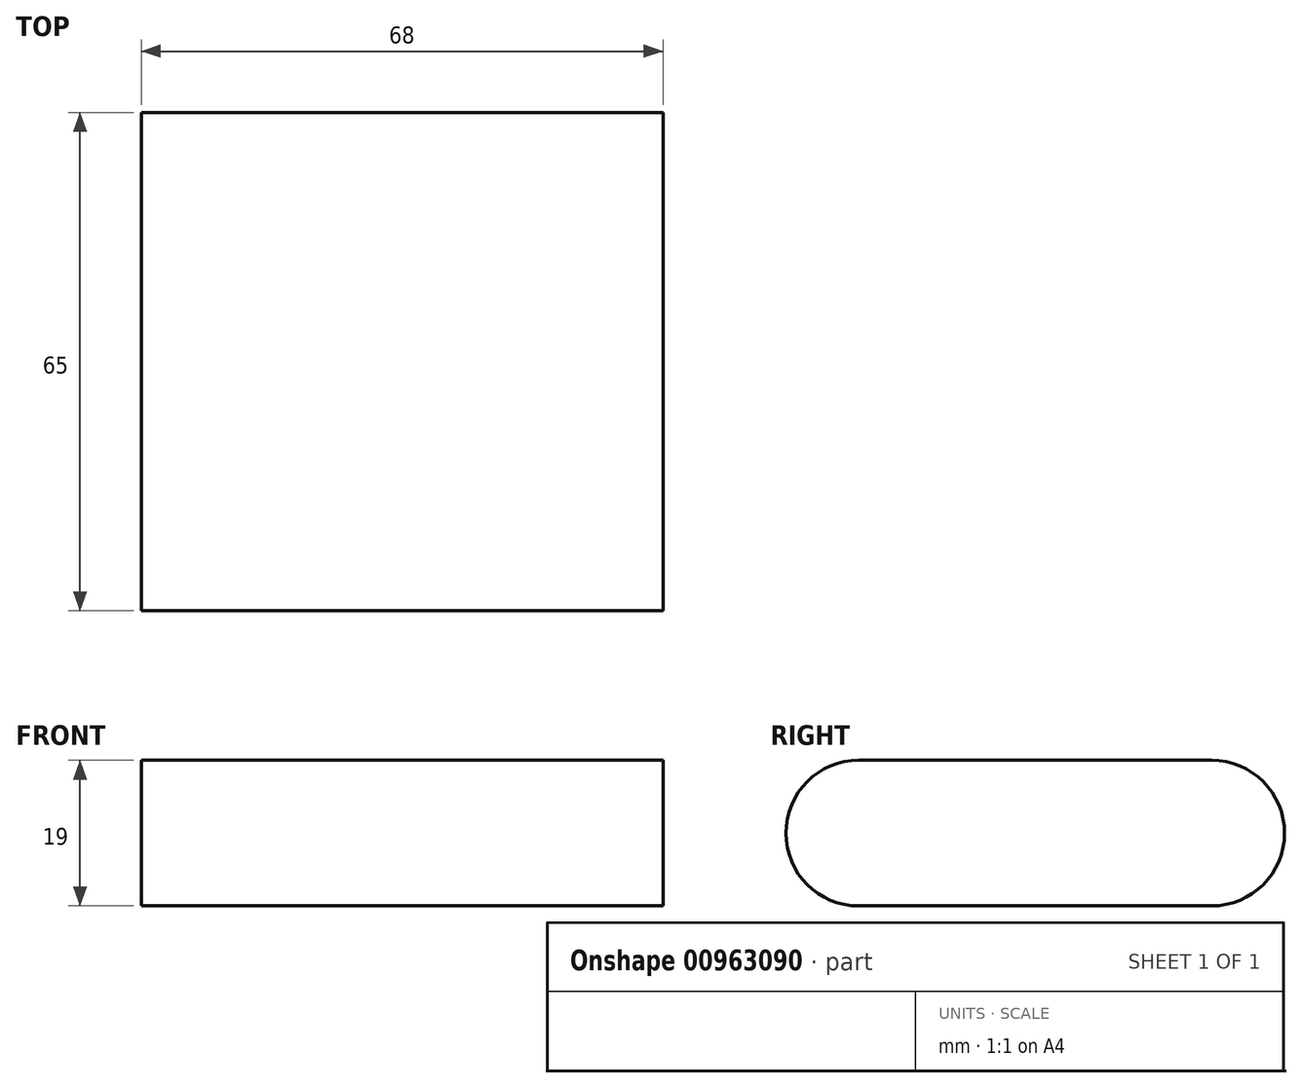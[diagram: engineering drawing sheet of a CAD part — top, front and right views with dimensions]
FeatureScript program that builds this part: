
annotation { "Feature Type Name" : "Feature", "Feature Type Description" : "" }
export const myFeature = defineFeature(function(context is Context, id is Id, definition is map)
    precondition{}
    {
        {
            var Q0;
            Q0=qCreatedBy(makeId("Right.planeOp"),FACE);
            var sketch = newSketch(context, id + "F0", { "sketchPlane" : qUnion([Q0])});
            skLineSegment(sketch, "E0.bottom", {"start": v(-32.5, 9.5) * mm, "end": v(32.5, 9.5) * mm});
            skLineSegment(sketch, "E0.top", {"start": v(-32.5, -9.5) * mm, "end": v(32.5, -9.5) * mm});
            skLineSegment(sketch, "E0.left", {"start": v(-32.5, 9.5) * mm, "end": v(-32.5, -9.5) * mm});
            skLineSegment(sketch, "E0.right", {"start": v(32.5, 9.5) * mm, "end": v(32.5, -9.5) * mm});
            skLineSegment(sketch, "E1", {"start": v(-32.5, 9.5) * mm, "end": v(32.5, -9.5) * mm, "construction": true});
            skSolve(sketch);
        }
        {
            var Q0;
            Q0 = qSketchRegion(id + "F0", true);
            extrude(context, id + "F1", {"entities" : qUnion([Q0]), "depth" : 68 * mm, "offsetDistance" : 25 * mm, "symmetric" : true});
        }
        {
            var Q0;
            Q0=makeQuery(id+"F1.opExtrude","SWEPT_EDGE",EDGE,{"disambiguationData":[OSD([sQuery(id+"F0.wireOp",EDGE,"E0.bottom"),sQuery(id+"F0.wireOp",EDGE,"E0.left")])]});
            var Q1;
            Q1=makeQuery(id+"F1.opExtrude","SWEPT_EDGE",EDGE,{"disambiguationData":[OSD([sQuery(id+"F0.wireOp",EDGE,"E0.top"),sQuery(id+"F0.wireOp",EDGE,"E0.left")])]});
            var Q2;
            Q2=makeQuery(id+"F1.opExtrude","SWEPT_EDGE",EDGE,{"disambiguationData":[OSD([sQuery(id+"F0.wireOp",EDGE,"E0.bottom"),sQuery(id+"F0.wireOp",EDGE,"E0.right")])]});
            var Q3;
            Q3=makeQuery(id+"F1.opExtrude","SWEPT_EDGE",EDGE,{"disambiguationData":[OSD([sQuery(id+"F0.wireOp",EDGE,"E0.top"),sQuery(id+"F0.wireOp",EDGE,"E0.right")])]});
            fillet(context, id + "F2", {"entities" : qUnion([Q0, Q1, Q2, Q3]), "tangentPropagation" : true, "radius" : (19 / 2) * mm, "defaultsChanged" : false, "vertexSettings" : [], "allowEdgeOverflow" : false});
        }
    });
